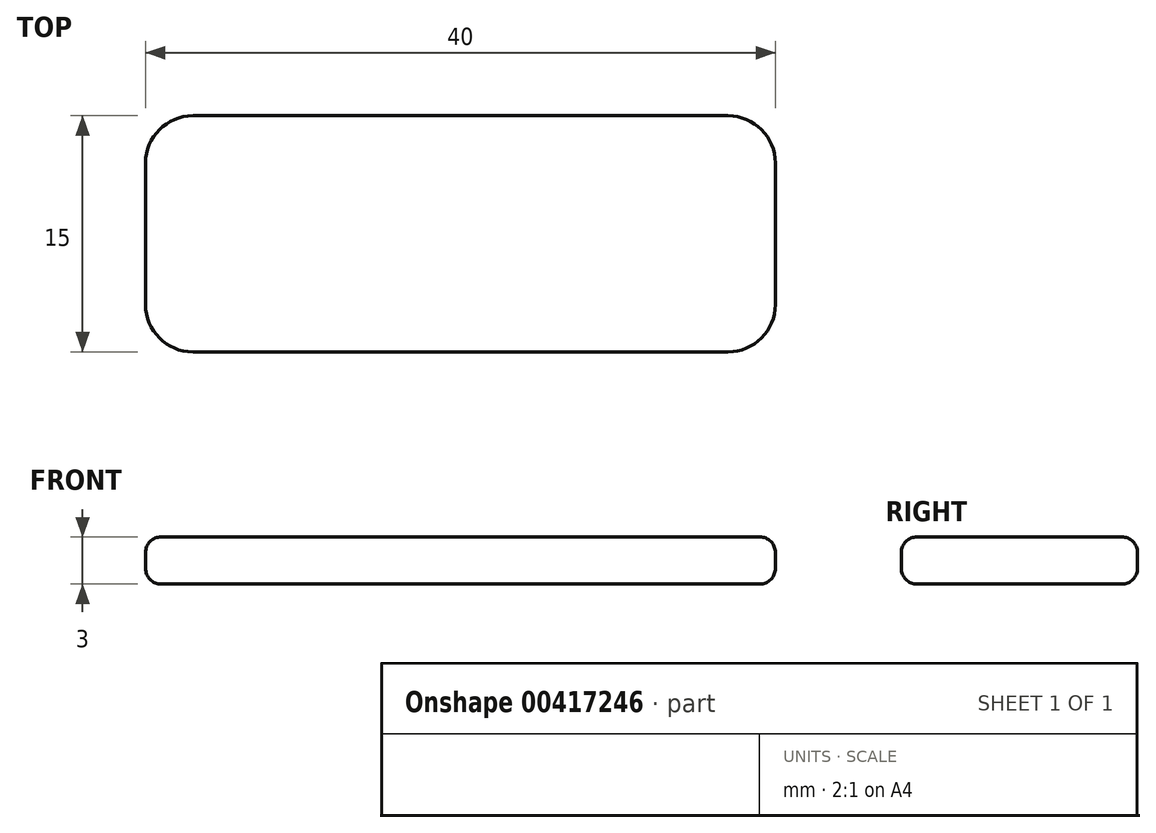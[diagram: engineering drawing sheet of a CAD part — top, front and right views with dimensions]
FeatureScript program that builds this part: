
annotation { "Feature Type Name" : "Feature", "Feature Type Description" : "" }
export const myFeature = defineFeature(function(context is Context, id is Id, definition is map)
    precondition{}
    {
        {
            var Q0;
            Q0=qCreatedBy(makeId("Top.planeOp"),FACE);
            var sketch = newSketch(context, id + "F0", { "sketchPlane" : qUnion([Q0])});
            skLineSegment(sketch, "E0.bottom", {"start": v(17, 7.5) * mm, "end": v(-17, 7.5) * mm});
            skLineSegment(sketch, "E0.top", {"start": v(17, -7.5) * mm, "end": v(-17, -7.5) * mm});
            skLineSegment(sketch, "E0.left", {"start": v(20, 4.5) * mm, "end": v(20, -4.5) * mm});
            skLineSegment(sketch, "E0.right", {"start": v(-20, 4.5) * mm, "end": v(-20, -4.5) * mm});
            skPoint(sketch, "E0.middle", {"position": v(0, 0) * mm});
            skPoint(sketch, "E1.visualSharp", {"position": v(-20, 7.5) * mm});
            skArc(sketch, "E1.filletArc", {"start": v(-17, 7.5) * mm, "mid": v(-19.12, 6.62) * mm, "end": v(-20, 4.5) * mm});
            skPoint(sketch, "E2.visualSharp", {"position": v(-20, -7.5) * mm});
            skArc(sketch, "E2.filletArc", {"start": v(-20, -4.5) * mm, "mid": v(-19.12, -6.62) * mm, "end": v(-17, -7.5) * mm});
            skPoint(sketch, "E3.visualSharp", {"position": v(20, 7.5) * mm});
            skArc(sketch, "E3.filletArc", {"start": v(20, 4.5) * mm, "mid": v(19.12, 6.62) * mm, "end": v(17, 7.5) * mm});
            skPoint(sketch, "E4.visualSharp", {"position": v(20, -7.5) * mm});
            skArc(sketch, "E4.filletArc", {"start": v(17, -7.5) * mm, "mid": v(19.12, -6.62) * mm, "end": v(20, -4.5) * mm});
            skSolve(sketch);
        }
        {
            var Q0;
            Q0 = qSketchRegion(id + "F0", true);
            extrude(context, id + "F1", {"entities" : qUnion([Q0]), "oppositeDirection" : true, "depth" : 3 * mm});
        }
        {
            var Q0;
            Q0=makeQuery(id+"F1.opExtrude","CAP_FACE",FACE,{"disambiguationData":[OSD([sQuery(id+"F0.wireOp",EDGE,"E0.bottom"),sQuery(id+"F0.wireOp",EDGE,"E0.top"),sQuery(id+"F0.wireOp",EDGE,"E0.left"),sQuery(id+"F0.wireOp",EDGE,"E0.right"),sQuery(id+"F0.wireOp",EDGE,"E1.filletArc"),sQuery(id+"F0.wireOp",EDGE,"E2.filletArc"),sQuery(id+"F0.wireOp",EDGE,"E3.filletArc"),sQuery(id+"F0.wireOp",EDGE,"E4.filletArc")])],"isStart":true});
            var Q1;
            Q1=makeQuery(id+"F1.opExtrude","CAP_FACE",FACE,{"disambiguationData":[OSD([sQuery(id+"F0.wireOp",EDGE,"E0.bottom"),sQuery(id+"F0.wireOp",EDGE,"E0.top"),sQuery(id+"F0.wireOp",EDGE,"E0.left"),sQuery(id+"F0.wireOp",EDGE,"E0.right"),sQuery(id+"F0.wireOp",EDGE,"E1.filletArc"),sQuery(id+"F0.wireOp",EDGE,"E2.filletArc"),sQuery(id+"F0.wireOp",EDGE,"E3.filletArc"),sQuery(id+"F0.wireOp",EDGE,"E4.filletArc")])],"isStart":false});
            fillet(context, id + "F2", {"entities" : qUnion([Q0, Q1]), "radius" : 1 * mm, "tangentPropagation" : true, "allowEdgeOverflow" : false});
        }
    });
